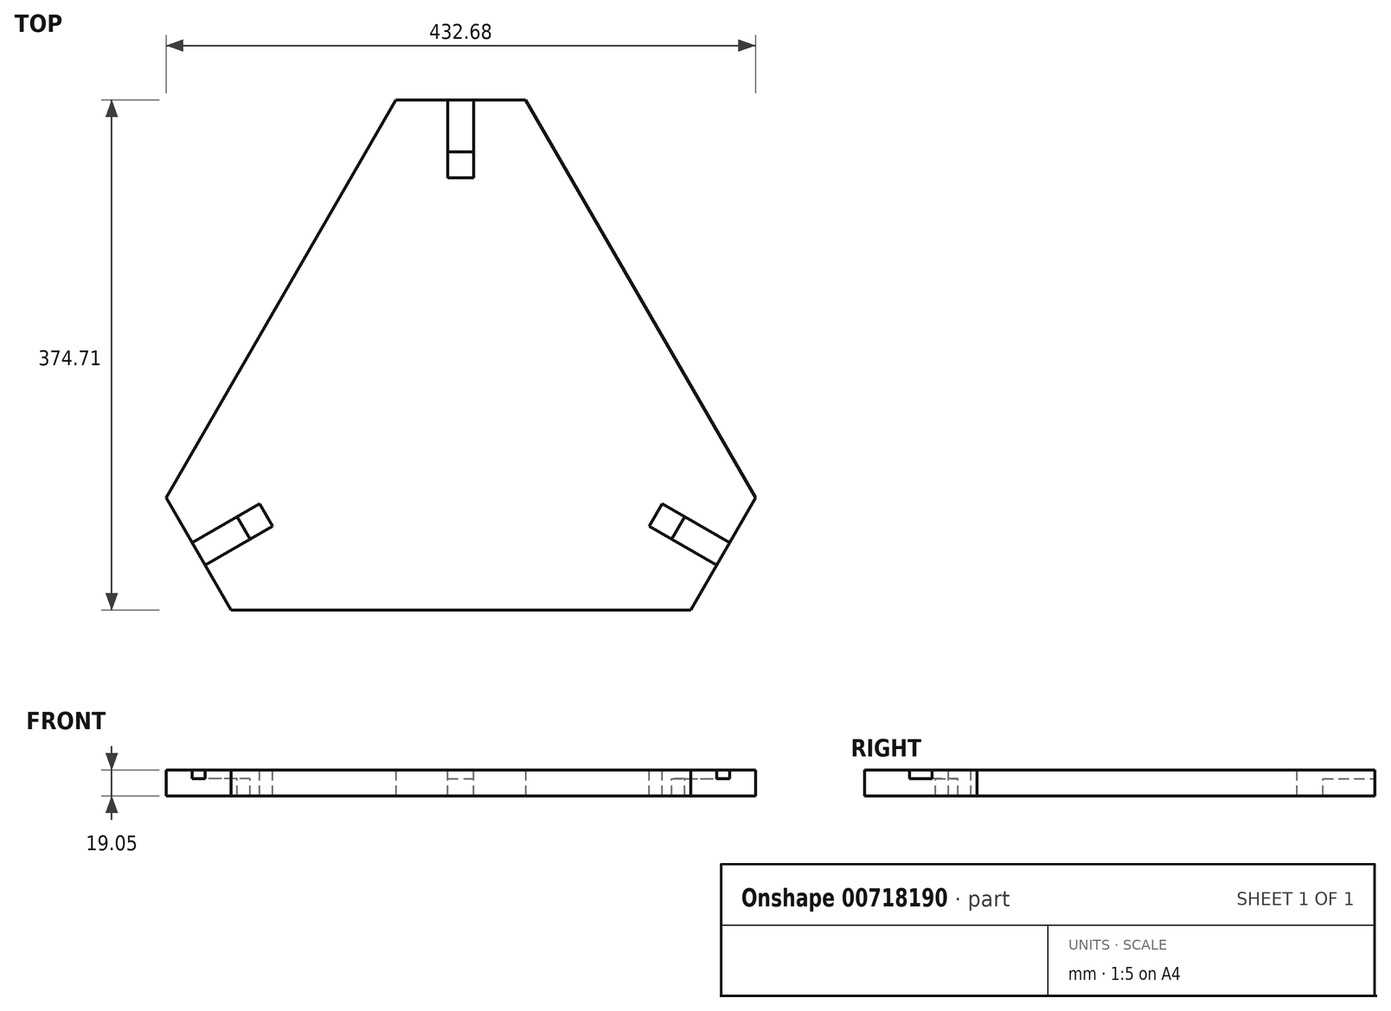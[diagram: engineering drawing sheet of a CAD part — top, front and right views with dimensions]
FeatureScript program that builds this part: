
annotation { "Feature Type Name" : "Feature", "Feature Type Description" : "" }
export const myFeature = defineFeature(function(context is Context, id is Id, definition is map)
    precondition{}
    {
        {
            var Q0;
            Q0=qCreatedBy(makeId("Top.planeOp"),FACE);
            var sketch = newSketch(context, id + "F0", { "sketchPlane" : qUnion([Q0])});
            skLineSegment(sketch, "E0", {"start": v(-47.63, 222.31) * mm, "end": v(47.63, 222.31) * mm});
            skLineSegment(sketch, "E1", {"start": v(47.63, 222.31) * mm, "end": v(216.34, -69.91) * mm});
            skLineSegment(sketch, "E2", {"start": v(216.34, -69.91) * mm, "end": v(168.71, -152.4) * mm});
            skLineSegment(sketch, "E3", {"start": v(168.71, -152.4) * mm, "end": v(-168.71, -152.4) * mm});
            skLineSegment(sketch, "E4", {"start": v(-168.71, -152.4) * mm, "end": v(-216.34, -69.91) * mm});
            skLineSegment(sketch, "E5", {"start": v(-216.34, -69.91) * mm, "end": v(-47.62, 222.31) * mm});
            skLineSegment(sketch, "E6", {"start": v(0, 0) * mm, "end": v(0, 222.31) * mm, "construction": true});
            skLineSegment(sketch, "E7", {"start": v(0, 0) * mm, "end": v(192.53, -111.16) * mm, "construction": true});
            skLineSegment(sketch, "E8", {"start": v(-192.53, -111.16) * mm, "end": v(0, 0) * mm, "construction": true});
            skSolve(sketch);
        }
        {
            var Q0;
            Q0 = qSketchRegion(id + "F0", true);
            extrude(context, id + "F1", {"entities" : qUnion([Q0]), "depth" : 19.05 * mm, "offsetDistance" : 25.4 * mm});
        }
        {
            var Q0;
            Q0=makeQuery(id+"F1.opExtrude","CAP_FACE",FACE,{"disambiguationData":[OSD([sQuery(id+"F0.wireOp",EDGE,"E0"),sQuery(id+"F0.wireOp",EDGE,"E1"),sQuery(id+"F0.wireOp",EDGE,"E2"),sQuery(id+"F0.wireOp",EDGE,"E3"),sQuery(id+"F0.wireOp",EDGE,"E4"),sQuery(id+"F0.wireOp",EDGE,"E5")])],"isStart":false});
            var sketch = newSketch(context, id + "F2", { "sketchPlane" : qUnion([Q0])});
            skLineSegment(sketch, "E9", {"start": v(0, 0) * mm, "end": v(0, 222.31) * mm, "construction": true});
            skLineSegment(sketch, "E10", {"start": v(-192.53, -111.16) * mm, "end": v(0, 0) * mm, "construction": true});
            skLineSegment(sketch, "E11", {"start": v(0, 0) * mm, "end": v(192.53, -111.16) * mm, "construction": true});
            skPoint(sketch, "E11.endSnap0", {"position": v(192.53, -111.16) * mm});
            skLineSegment(sketch, "E12.bottom", {"start": v(9.52, 165.16) * mm, "end": v(-9.53, 165.16) * mm});
            skLineSegment(sketch, "E12.top", {"start": v(9.52, 184.21) * mm, "end": v(-9.53, 184.21) * mm});
            skLineSegment(sketch, "E12.left", {"start": v(9.52, 165.16) * mm, "end": v(9.52, 184.21) * mm});
            skLineSegment(sketch, "E12.right", {"start": v(-9.53, 165.16) * mm, "end": v(-9.53, 184.21) * mm});
            skPoint(sketch, "E12.middle", {"position": v(0, 174.69) * mm});
            skLineSegment(sketch, "E13.bottom", {"start": v(164.3, -83.86) * mm, "end": v(154.77, -100.35) * mm});
            skLineSegment(sketch, "E13.top", {"start": v(147.8, -74.33) * mm, "end": v(138.27, -90.83) * mm});
            skLineSegment(sketch, "E13.left", {"start": v(164.3, -83.86) * mm, "end": v(147.8, -74.33) * mm});
            skLineSegment(sketch, "E13.right", {"start": v(154.77, -100.35) * mm, "end": v(138.27, -90.83) * mm});
            skPoint(sketch, "E13.middle", {"position": v(151.28, -87.34) * mm});
            skLineSegment(sketch, "E14.bottom", {"start": v(-154.77, -100.35) * mm, "end": v(-164.3, -83.86) * mm});
            skLineSegment(sketch, "E14.top", {"start": v(-138.27, -90.83) * mm, "end": v(-147.8, -74.33) * mm});
            skLineSegment(sketch, "E14.left", {"start": v(-154.77, -100.35) * mm, "end": v(-138.27, -90.83) * mm});
            skLineSegment(sketch, "E14.right", {"start": v(-164.3, -83.86) * mm, "end": v(-147.8, -74.33) * mm});
            skPoint(sketch, "E14.middle", {"position": v(-151.28, -87.34) * mm});
            skSolve(sketch);
        }
        {
            var Q0;
            Q0 = qSketchRegion(id + "F2", true);
            extrude(context, id + "F3", {"entities" : qUnion([Q0]), "operationType" : NewBodyOperationType.REMOVE, "endBound" : BoundingType.UP_TO_NEXT, "oppositeDirection" : true, "depth" : 25.4 * mm, "offsetDistance" : 25.4 * mm});
        }
        {
            var Q0;
            Q0=makeQuery(id+"F1.opExtrude","CAP_FACE",FACE,{"disambiguationData":[OSD([sQuery(id+"F0.wireOp",EDGE,"E0"),sQuery(id+"F0.wireOp",EDGE,"E1"),sQuery(id+"F0.wireOp",EDGE,"E2"),sQuery(id+"F0.wireOp",EDGE,"E3"),sQuery(id+"F0.wireOp",EDGE,"E4"),sQuery(id+"F0.wireOp",EDGE,"E5")])],"isStart":false});
            var sketch = newSketch(context, id + "F4", { "sketchPlane" : qUnion([Q0])});
            skLineSegment(sketch, "E15", {"start": v(-164.3, -83.86) * mm, "end": v(-197.29, -102.9) * mm});
            skLineSegment(sketch, "E16", {"start": v(-154.77, -100.35) * mm, "end": v(-187.76, -119.4) * mm});
            skLineSegment(sketch, "E17", {"start": v(-187.76, -119.4) * mm, "end": v(-197.29, -102.9) * mm});
            skLineSegment(sketch, "E18", {"start": v(-164.3, -83.86) * mm, "end": v(-154.77, -100.35) * mm});
            skLineSegment(sketch, "E19", {"start": v(164.3, -83.86) * mm, "end": v(197.29, -102.9) * mm});
            skLineSegment(sketch, "E20", {"start": v(154.77, -100.35) * mm, "end": v(187.76, -119.4) * mm});
            skLineSegment(sketch, "E21", {"start": v(197.29, -102.9) * mm, "end": v(187.76, -119.4) * mm});
            skLineSegment(sketch, "E22", {"start": v(164.3, -83.86) * mm, "end": v(154.77, -100.35) * mm});
            skLineSegment(sketch, "E23", {"start": v(-9.53, 184.21) * mm, "end": v(-9.53, 222.31) * mm});
            skLineSegment(sketch, "E24", {"start": v(9.52, 184.21) * mm, "end": v(9.52, 222.31) * mm});
            skLineSegment(sketch, "E25", {"start": v(-9.53, 222.31) * mm, "end": v(9.52, 222.31) * mm});
            skLineSegment(sketch, "E26", {"start": v(-9.53, 184.21) * mm, "end": v(9.52, 184.21) * mm});
            skSolve(sketch);
        }
        {
            var Q0;
            Q0 = qSketchRegion(id + "F4", true);
            extrude(context, id + "F5", {"entities" : qUnion([Q0]), "operationType" : NewBodyOperationType.REMOVE, "oppositeDirection" : true, "depth" : 6.35 * mm, "offsetDistance" : 25.4 * mm});
        }
    });
